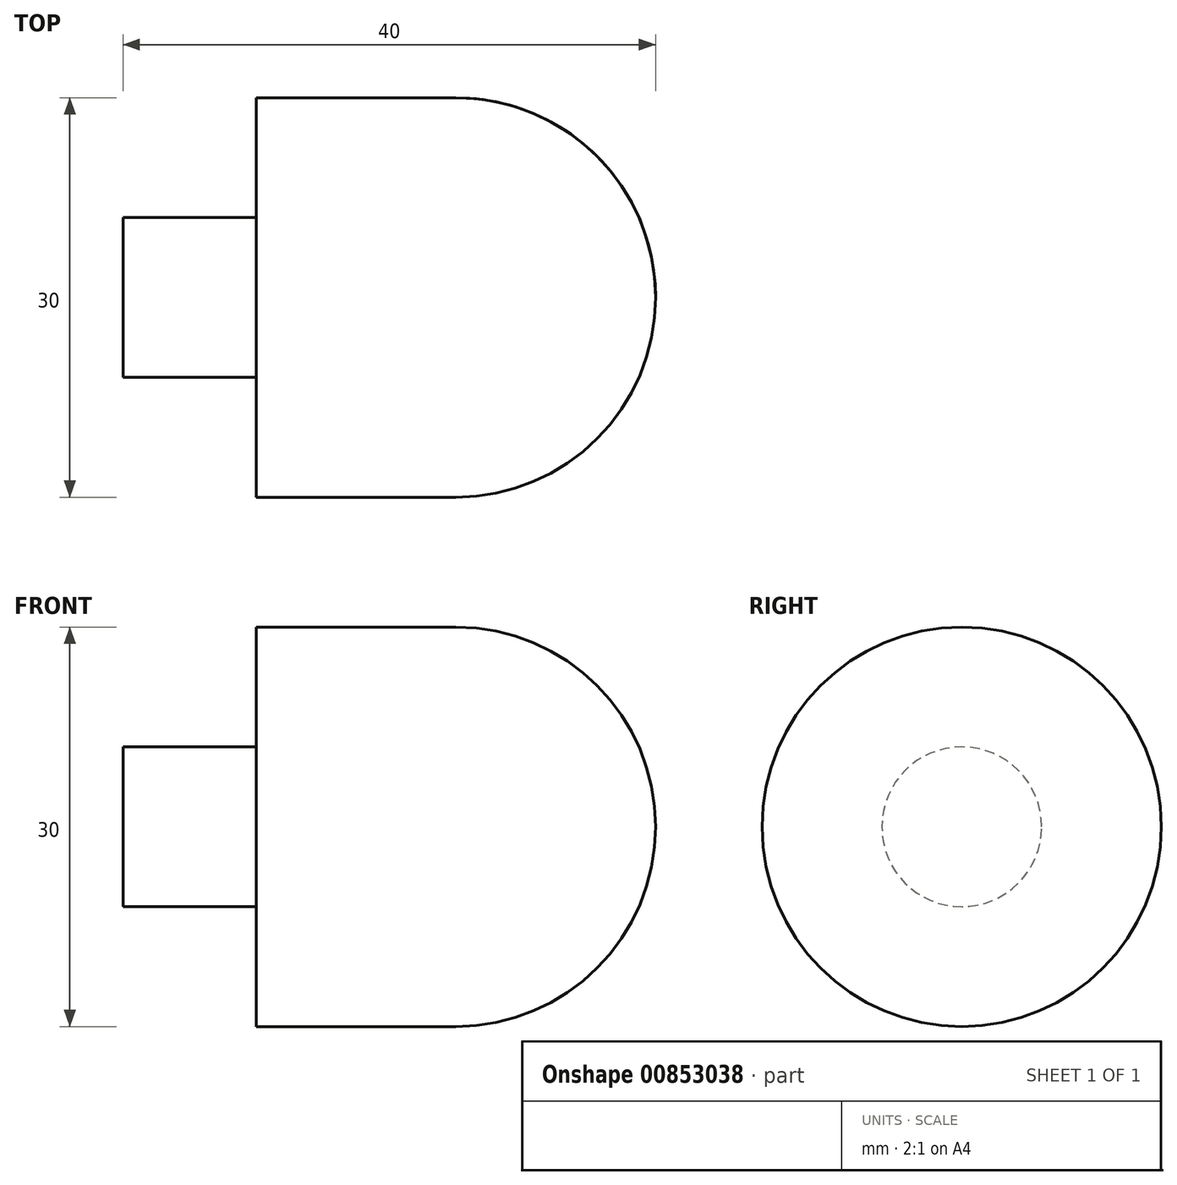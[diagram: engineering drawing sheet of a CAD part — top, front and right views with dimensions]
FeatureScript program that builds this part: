
annotation { "Feature Type Name" : "Feature", "Feature Type Description" : "" }
export const myFeature = defineFeature(function(context is Context, id is Id, definition is map)
    precondition{}
    {
        {
            var Q0;
            Q0=qCreatedBy(makeId("Top.planeOp"),FACE);
            var sketch = newSketch(context, id + "F0", { "sketchPlane" : qUnion([Q0])});
            skLineSegment(sketch, "E0", {"start": v(15, 0) * mm, "end": v(-25, 0) * mm});
            skLineSegment(sketch, "E1", {"start": v(-25, 0) * mm, "end": v(-25, 6) * mm});
            skLineSegment(sketch, "E2", {"start": v(-25, 6) * mm, "end": v(-15, 6) * mm});
            skLineSegment(sketch, "E3", {"start": v(-15, 6) * mm, "end": v(-15, 15) * mm});
            skLineSegment(sketch, "E4", {"start": v(-15, 15) * mm, "end": v(0, 15) * mm});
            skArc(sketch, "E5", {"start": v(15, 0) * mm, "mid": v(10.6, 10.6) * mm, "end": v(0, 15) * mm});
            skSolve(sketch);
        }
        {
            var Q0;
            Q0=makeQuery(id+"F0.imprint","IMPRINT",FACE,{"disambiguationData":[TD([[makeQuery(id+"F0.imprint","IMPRINT",EDGE,{"derivedFrom":sQuery(id+"F0.wireOp",EDGE,"E0")}),-1.0]])]});
            var Q1;
            Q1=sQuery(id+"F0.wireOp",EDGE,"E0");
            revolve(context, id + "F1", {"surfaceOperationType" : NewSurfaceOperationType.NEW, "entities" : qUnion([Q0]), "axis" : qUnion([Q1]), "revolveType" : RevolveType.FULL});
        }
    });
